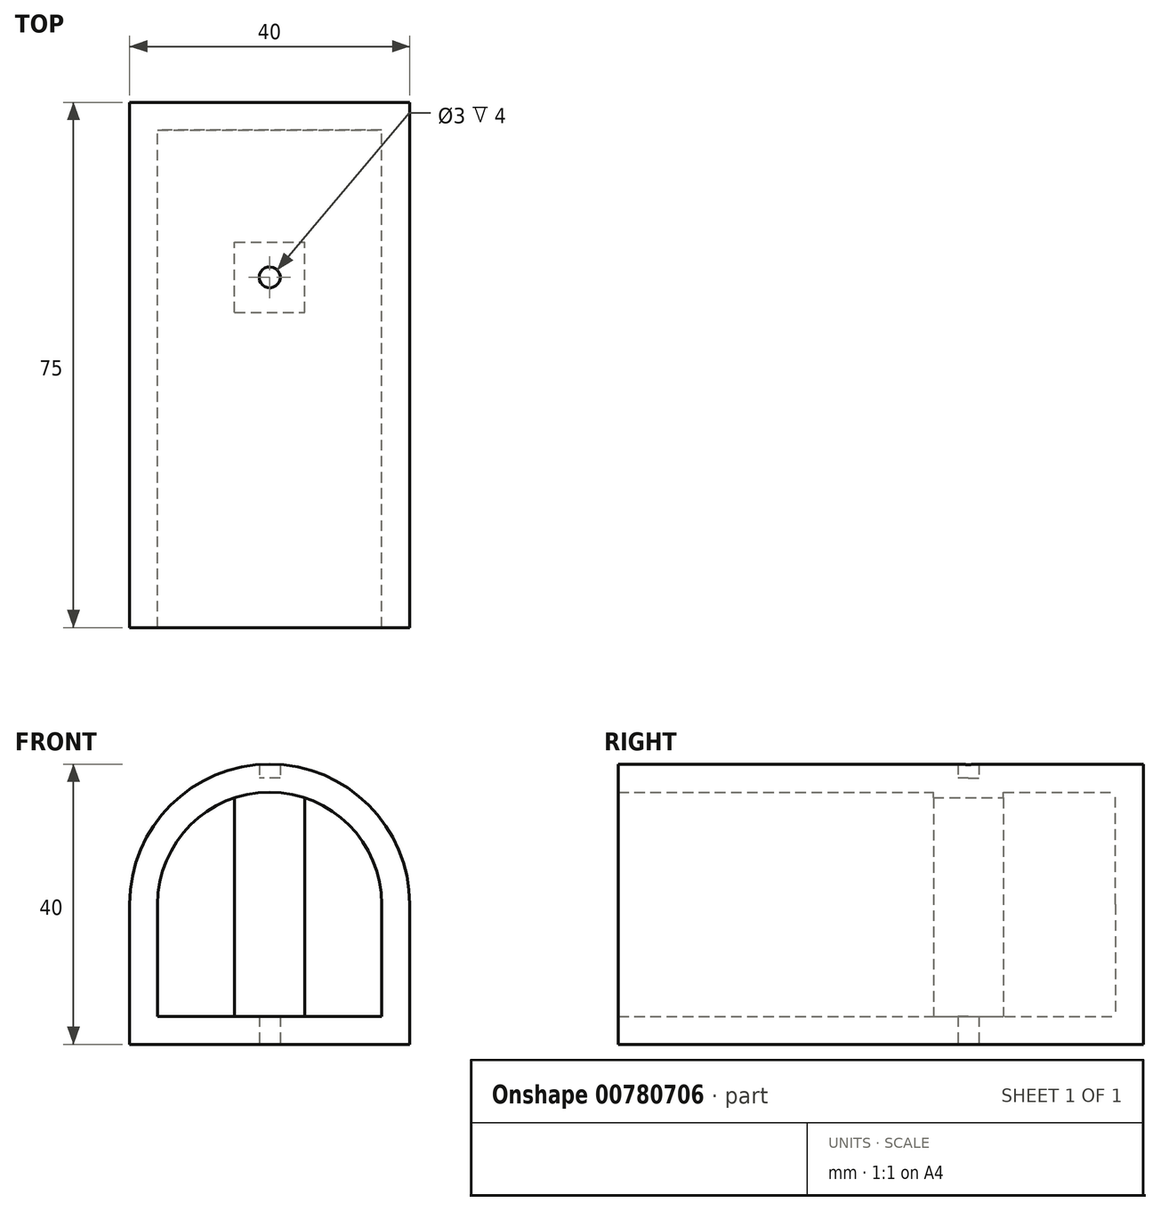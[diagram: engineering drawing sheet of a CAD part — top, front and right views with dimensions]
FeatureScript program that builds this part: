
annotation { "Feature Type Name" : "Feature", "Feature Type Description" : "" }
export const myFeature = defineFeature(function(context is Context, id is Id, definition is map)
    precondition{}
    {
        {
            var Q0;
            Q0=qCreatedBy(makeId("Front.planeOp"),FACE);
            var sketch = newSketch(context, id + "F0", { "sketchPlane" : qUnion([Q0])});
            skLineSegment(sketch, "E0", {"start": v(0, 0) * mm, "end": v(40, 0) * mm});
            skLineSegment(sketch, "E1", {"start": v(40, 0) * mm, "end": v(40, 40) * mm});
            skLineSegment(sketch, "E2", {"start": v(40, 40) * mm, "end": v(0, 40) * mm});
            skLineSegment(sketch, "E3", {"start": v(0, 40) * mm, "end": v(0, 0) * mm});
            skSolve(sketch);
        }
        {
            var Q0;
            Q0 = qSketchRegion(id + "F0", true);
            extrude(context, id + "F1", {"entities" : qUnion([Q0]), "depth" : 75 * mm, "offsetDistance" : 25 * mm});
        }
        {
            var Q0;
            Q0=makeQuery(id+"F1.opExtrude","SWEPT_EDGE",EDGE,{"disambiguationData":[OSD([sQuery(id+"F0.wireOp",EDGE,"E1"),sQuery(id+"F0.wireOp",EDGE,"E2")])]});
            var Q1;
            Q1=makeQuery(id+"F1.opExtrude","SWEPT_EDGE",EDGE,{"disambiguationData":[OSD([sQuery(id+"F0.wireOp",EDGE,"E2"),sQuery(id+"F0.wireOp",EDGE,"E3")])]});
            fillet(context, id + "F2", {"entities" : qUnion([Q0, Q1]), "radius" : 20 * mm, "tangentPropagation" : true, "allowEdgeOverflow" : false});
        }
        {
            var Q0;
            Q0=makeQuery(id+"F1.opExtrude","CAP_FACE",FACE,{"disambiguationData":[OSD([sQuery(id+"F0.wireOp",EDGE,"E0"),sQuery(id+"F0.wireOp",EDGE,"E1"),sQuery(id+"F0.wireOp",EDGE,"E2"),sQuery(id+"F0.wireOp",EDGE,"E3")])],"isStart":false});
            shell(context, id + "F3", {"entities" : qUnion([Q0]), "thickness" : 4 * mm});
        }
        {
            var Q0;
            Q0=makeQuery(id+"F3.opShell","OFFSET_FACE",FACE,{"disambiguationData":[OSD([sQuery(id+"F0.wireOp",EDGE,"E0")])]});
            var sketch = newSketch(context, id + "F4", { "sketchPlane" : qUnion([Q0])});
            skLineSegment(sketch, "E4.bottom", {"start": v(15, -30) * mm, "end": v(25, -30) * mm});
            skLineSegment(sketch, "E4.top", {"start": v(15, -20) * mm, "end": v(25, -20) * mm});
            skLineSegment(sketch, "E4.left", {"start": v(15, -30) * mm, "end": v(15, -20) * mm});
            skLineSegment(sketch, "E4.right", {"start": v(25, -30) * mm, "end": v(25, -20) * mm});
            skSolve(sketch);
        }
        {
            var Q0;
            Q0=makeQuery(id+"F1.opExtrude","SWEPT_FACE",FACE,{"disambiguationData":[OSD([sQuery(id+"F0.wireOp",EDGE,"E0")])]});
            var sketch = newSketch(context, id + "F5", { "sketchPlane" : qUnion([Q0])});
            skCircle(sketch, "E5", {"center": v(20, 25) * mm, "radius": 1.5 * mm});
            skSolve(sketch);
        }
        {
            var Q0;
            Q0 = qSketchRegion(id + "F5", true);
            extrude(context, id + "F6", {"entities" : qUnion([Q0]), "operationType" : NewBodyOperationType.REMOVE, "endBound" : BoundingType.THROUGH_ALL, "oppositeDirection" : true, "depth" : 25 * mm, "offsetDistance" : 25 * mm});
        }
        {
            var Q0;
            Q0 = qSketchRegion(id + "F4", true);
            extrude(context, id + "F7", {"entities" : qUnion([Q0]), "operationType" : NewBodyOperationType.ADD, "depth" : 34 * mm, "offsetDistance" : 25 * mm});
        }
    });
